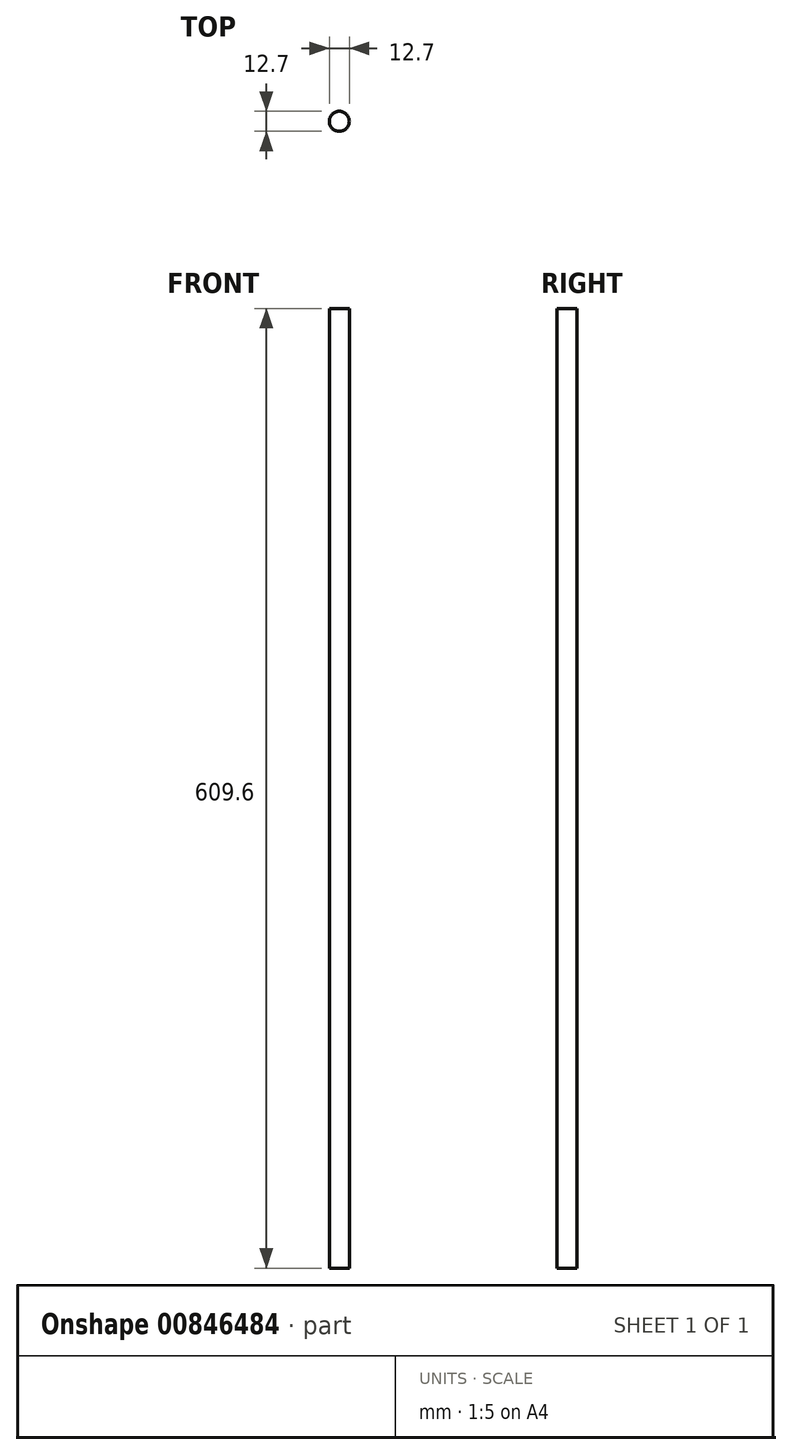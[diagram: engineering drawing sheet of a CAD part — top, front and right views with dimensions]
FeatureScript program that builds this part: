
annotation { "Feature Type Name" : "Feature", "Feature Type Description" : "" }
export const myFeature = defineFeature(function(context is Context, id is Id, definition is map)
    precondition{}
    {
        {
            var Q0;
            Q0=qCreatedBy(makeId("Top.planeOp"),FACE);
            var sketch = newSketch(context, id + "F0", { "sketchPlane" : qUnion([Q0])});
            skCircle(sketch, "E0", {"center": v(0, 0) * mm, "radius": 6.35 * mm});
            skSolve(sketch);
        }
        {
            var Q0;
            Q0 = qSketchRegion(id + "F0", true);
            extrude(context, id + "F1", {"entities" : qUnion([Q0]), "depth" : 609.6 * mm, "offsetDistance" : 25.4 * mm});
        }
    });
